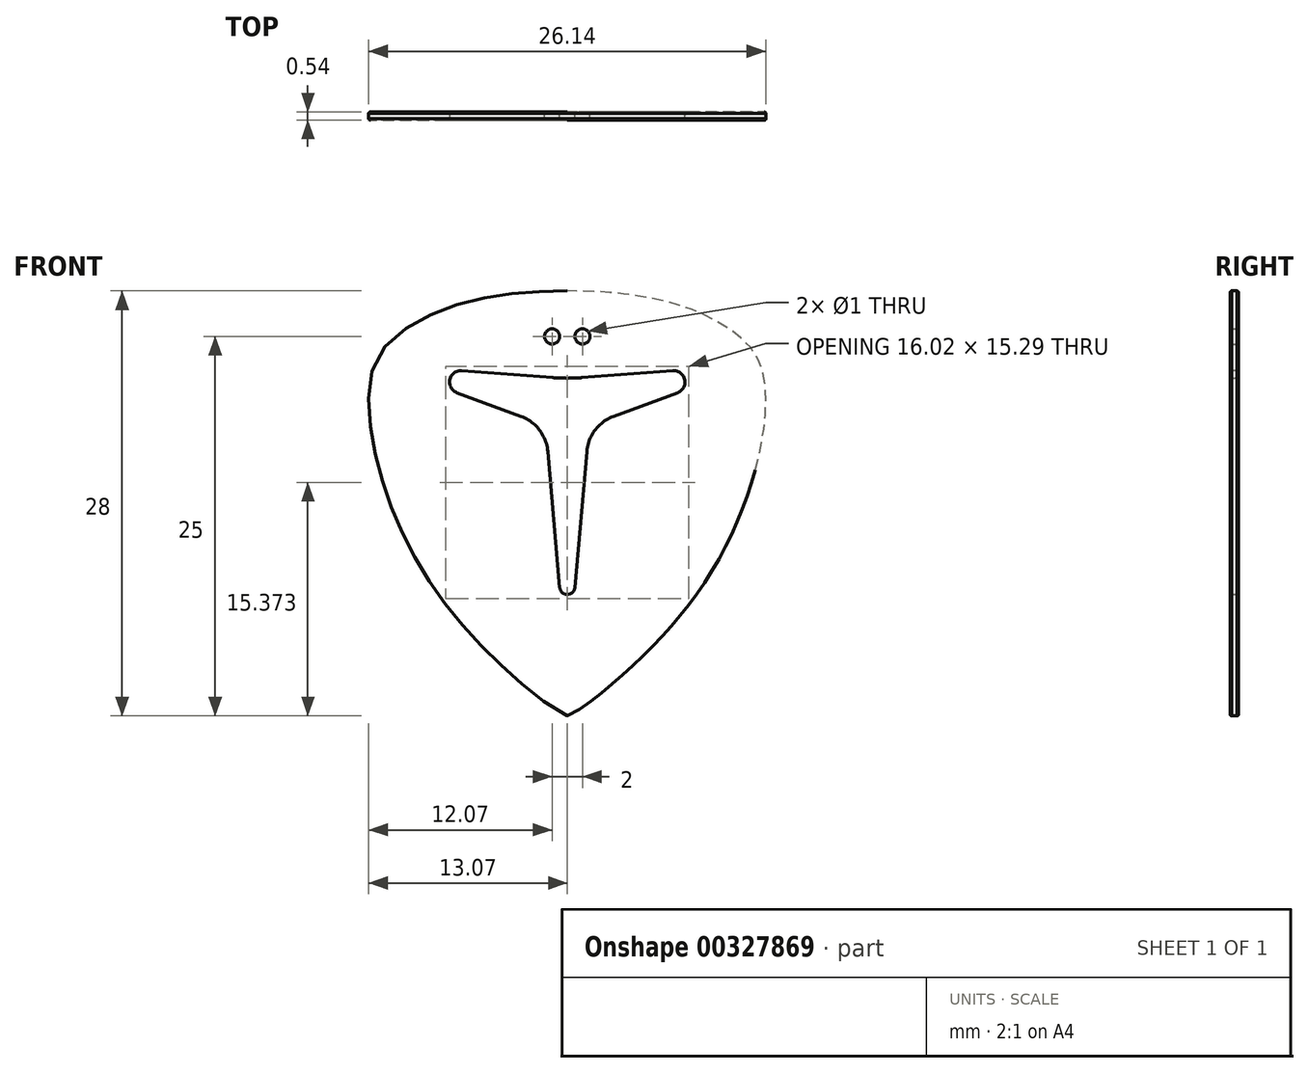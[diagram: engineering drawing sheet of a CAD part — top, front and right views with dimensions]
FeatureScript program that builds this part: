
annotation { "Feature Type Name" : "Feature", "Feature Type Description" : "" }
export const myFeature = defineFeature(function(context is Context, id is Id, definition is map)
    precondition{}
    {
        {
            var Q0;
            Q0=qCreatedBy(makeId("Front.planeOp"),FACE);
            var sketch = newSketch(context, id + "F0", { "sketchPlane" : qUnion([Q0])});
            skLineSegment(sketch, "E0", {"start": v(0, 0) * mm, "end": v(0, 6) * mm, "construction": true});
            skLineSegment(sketch, "E1", {"start": v(0, 0) * mm, "end": v(0, -22) * mm, "construction": true});
            skLineSegment(sketch, "E2", {"start": v(0, 0) * mm, "end": v(13, 0) * mm, "construction": true});
            skFitSpline(sketch, "E3", {"points": [v(0, -22) * mm, v(8.5, -14) * mm, v(13, 0) * mm, v(11, 3.25) * mm, v(0, 6) * mm], "startDerivative": vector(5.52, 0) * mm, "endDerivative": vector(-67.2, 0) * mm});
            skFitSpline(sketch, "E4.MirrorCS", {"points": [v(0, -22) * mm, v(-8.5, -14) * mm, v(-13, 0) * mm, v(-11, 3.25) * mm, v(0, 6) * mm], "startDerivative": vector(-5.52, 0) * mm, "endDerivative": vector(67.2, 0) * mm});
            skArc(sketch, "E5", {"start": v(7.26, -0.7) * mm, "mid": v(7.73, 0.16) * mm, "end": v(6.94, 0.75) * mm});
            skLineSegment(sketch, "E6", {"start": v(7.26, -0.7) * mm, "end": v(3.04, -2.27) * mm});
            skArc(sketch, "E7", {"start": v(3.04, -2.27) * mm, "mid": v(1.83, -3.17) * mm, "end": v(1.28, -4.58) * mm});
            skLineSegment(sketch, "E8", {"start": v(0.5, -13.54) * mm, "end": v(1.28, -4.58) * mm});
            skArc(sketch, "E9", {"start": v(0, -14) * mm, "mid": v(0.34, -13.87) * mm, "end": v(0.5, -13.54) * mm});
            skArc(sketch, "E10.MirrorCS", {"start": v(0, -14) * mm, "mid": v(-0.34, -13.87) * mm, "end": v(-0.5, -13.54) * mm});
            skLineSegment(sketch, "E11.MirrorCS", {"start": v(-0.5, -13.54) * mm, "end": v(-1.28, -4.58) * mm});
            skArc(sketch, "E12.MirrorCS", {"start": v(-3.04, -2.27) * mm, "mid": v(-1.83, -3.17) * mm, "end": v(-1.28, -4.58) * mm});
            skLineSegment(sketch, "E13.MirrorCS", {"start": v(-7.26, -0.7) * mm, "end": v(-3.04, -2.27) * mm});
            skArc(sketch, "E14.MirrorCS", {"start": v(-7.26, -0.7) * mm, "mid": v(-7.73, 0.16) * mm, "end": v(-6.94, 0.75) * mm});
            skLineSegment(sketch, "E15", {"start": v(6.94, 0.75) * mm, "end": v(0.96, 0.29) * mm});
            skArc(sketch, "E16", {"start": v(0, 0.25) * mm, "mid": v(0.48, 0.26) * mm, "end": v(0.96, 0.29) * mm});
            skArc(sketch, "E17.MirrorCS", {"start": v(0, 0.25) * mm, "mid": v(-0.48, 0.26) * mm, "end": v(-0.96, 0.29) * mm});
            skLineSegment(sketch, "E18.MirrorCS", {"start": v(-6.94, 0.75) * mm, "end": v(-0.96, 0.29) * mm});
            skLineSegment(sketch, "E19", {"start": v(0, 3) * mm, "end": v(1, 3) * mm});
            skCircle(sketch, "E20", {"center": v(1, 3) * mm, "radius": 0.5 * mm});
            skCircle(sketch, "E21.MirrorC", {"center": v(-1, 3) * mm, "radius": 0.5 * mm});
            skLineSegment(sketch, "E22.MirrorCS", {"start": v(0, 3) * mm, "end": v(-1, 3) * mm});
            skSolve(sketch);
        }
        {
            var Q0;
            Q0=qSketchRegion(id+"F0",true);
            extrude(context, id + "F1", {"entities" : qUnion([Q0]), "depth" : 0.54 * mm});
        }
        {
            var Q0;
            Q0=makeQuery(id+"F1.opExtrude","CAP_EDGE",EDGE,{"disambiguationData":[OSD([sQuery(id+"F0.wireOp",EDGE,"E5")])],"isStart":false});
            var Q1;
            Q1=makeQuery(id+"F1.opExtrude","CAP_EDGE",EDGE,{"disambiguationData":[OSD([sQuery(id+"F0.wireOp",EDGE,"E7")])],"isStart":true});
            var Q2;
            Q2=makeQuery(id+"F1.opExtrude","CAP_EDGE",EDGE,{"disambiguationData":[OSD([sQuery(id+"F0.wireOp",EDGE,"E9"),sQuery(id+"F0.wireOp",EDGE,"E10.MirrorCS")])],"isStart":false});
            var Q3;
            Q3=makeQuery(id+"F1.opExtrude","CAP_EDGE",EDGE,{"disambiguationData":[OSD([sQuery(id+"F0.wireOp",EDGE,"E14.MirrorCS")])],"isStart":false});
            var Q4;
            Q4=makeQuery(id+"F1.opExtrude","CAP_EDGE",EDGE,{"disambiguationData":[OSD([sQuery(id+"F0.wireOp",EDGE,"E5")])],"isStart":true});
            var Q5;
            Q5=makeQuery(id+"F1.opExtrude","CAP_EDGE",EDGE,{"disambiguationData":[OSD([sQuery(id+"F0.wireOp",EDGE,"E12.MirrorCS")])],"isStart":false});
            var Q6;
            Q6=makeQuery(id+"F1.opExtrude","CAP_EDGE",EDGE,{"disambiguationData":[OSD([sQuery(id+"F0.wireOp",EDGE,"E7")])],"isStart":false});
            var Q7;
            Q7=makeQuery(id+"F1.opExtrude","CAP_EDGE",EDGE,{"disambiguationData":[OSD([sQuery(id+"F0.wireOp",EDGE,"cP70XH3B-hxny-nh1n-TbyW-52Zl4TOD4HrO"),sQuery(id+"F0.wireOp",EDGE,"9cf6c757-e815-40dd-95a7-672993b90d513.MirrorCS")])],"isStart":true});
            var Q8;
            Q8=makeQuery(id+"F1.opExtrude","CAP_EDGE",EDGE,{"disambiguationData":[OSD([sQuery(id+"F0.wireOp",EDGE,"E13.MirrorCS")])],"isStart":false});
            var Q9;
            Q9=makeQuery(id+"F1.opExtrude","CAP_EDGE",EDGE,{"disambiguationData":[OSD([sQuery(id+"F0.wireOp",EDGE,"E12.MirrorCS")])],"isStart":true});
            var Q10;
            Q10=makeQuery(id+"F1.opExtrude","CAP_EDGE",EDGE,{"disambiguationData":[OSD([sQuery(id+"F0.wireOp",EDGE,"cP70XH3B-hxny-nh1n-TbyW-52Zl4TOD4HrO"),sQuery(id+"F0.wireOp",EDGE,"9cf6c757-e815-40dd-95a7-672993b90d513.MirrorCS")])],"isStart":false});
            var Q11;
            Q11=makeQuery(id+"F1.opExtrude","CAP_EDGE",EDGE,{"disambiguationData":[OSD([sQuery(id+"F0.wireOp",EDGE,"E9"),sQuery(id+"F0.wireOp",EDGE,"E10.MirrorCS")])],"isStart":true});
            var Q12;
            Q12=makeQuery(id+"F1.opExtrude","SWEPT_EDGE",EDGE,{"disambiguationData":[OSD([sQuery(id+"F0.wireOp",EDGE,"9cf6c757-e815-40dd-95a7-672993b90d513.MirrorCS"),sQuery(id+"F0.wireOp",EDGE,"E14.MirrorCS")])]});
            var Q13;
            Q13=makeQuery(id+"F1.opExtrude","CAP_EDGE",EDGE,{"disambiguationData":[OSD([sQuery(id+"F0.wireOp",EDGE,"E8")])],"isStart":true});
            var Q14;
            Q14=makeQuery(id+"F1.opExtrude","CAP_EDGE",EDGE,{"disambiguationData":[OSD([sQuery(id+"F0.wireOp",EDGE,"E11.MirrorCS")])],"isStart":false});
            var Q15;
            Q15=makeQuery(id+"F1.opExtrude","SWEPT_EDGE",EDGE,{"disambiguationData":[OSD([sQuery(id+"F0.wireOp",EDGE,"E6"),sQuery(id+"F0.wireOp",EDGE,"E7")])]});
            var Q16;
            Q16=makeQuery(id+"F1.opExtrude","SWEPT_EDGE",EDGE,{"disambiguationData":[OSD([sQuery(id+"F0.wireOp",EDGE,"E8"),sQuery(id+"F0.wireOp",EDGE,"E9")])]});
            var Q17;
            Q17=makeQuery(id+"F1.opExtrude","SWEPT_EDGE",EDGE,{"disambiguationData":[OSD([sQuery(id+"F0.wireOp",EDGE,"E13.MirrorCS"),sQuery(id+"F0.wireOp",EDGE,"E14.MirrorCS")])]});
            var Q18;
            Q18=makeQuery(id+"F1.opExtrude","SWEPT_EDGE",EDGE,{"disambiguationData":[OSD([sQuery(id+"F0.wireOp",EDGE,"E10.MirrorCS"),sQuery(id+"F0.wireOp",EDGE,"E11.MirrorCS")])]});
            var Q19;
            Q19=makeQuery(id+"F1.opExtrude","SWEPT_EDGE",EDGE,{"disambiguationData":[OSD([sQuery(id+"F0.wireOp",EDGE,"E11.MirrorCS"),sQuery(id+"F0.wireOp",EDGE,"E12.MirrorCS")])]});
            var Q20;
            Q20=makeQuery(id+"F1.opExtrude","SWEPT_EDGE",EDGE,{"disambiguationData":[OSD([sQuery(id+"F0.wireOp",EDGE,"E5"),sQuery(id+"F0.wireOp",EDGE,"E6")])]});
            var Q21;
            Q21=makeQuery(id+"F1.opExtrude","CAP_EDGE",EDGE,{"disambiguationData":[OSD([sQuery(id+"F0.wireOp",EDGE,"E14.MirrorCS")])],"isStart":true});
            var Q22;
            Q22=makeQuery(id+"F1.opExtrude","SWEPT_EDGE",EDGE,{"disambiguationData":[OSD([sQuery(id+"F0.wireOp",EDGE,"E12.MirrorCS"),sQuery(id+"F0.wireOp",EDGE,"E13.MirrorCS")])]});
            var Q23;
            Q23=makeQuery(id+"F1.opExtrude","CAP_EDGE",EDGE,{"disambiguationData":[OSD([sQuery(id+"F0.wireOp",EDGE,"E8")])],"isStart":false});
            var Q24;
            Q24=makeQuery(id+"F1.opExtrude","SWEPT_EDGE",EDGE,{"disambiguationData":[OSD([sQuery(id+"F0.wireOp",EDGE,"cP70XH3B-hxny-nh1n-TbyW-52Zl4TOD4HrO"),sQuery(id+"F0.wireOp",EDGE,"E5")])]});
            var Q25;
            Q25=makeQuery(id+"F1.opExtrude","CAP_EDGE",EDGE,{"disambiguationData":[OSD([sQuery(id+"F0.wireOp",EDGE,"E6")])],"isStart":false});
            var Q26;
            Q26=makeQuery(id+"F1.opExtrude","CAP_EDGE",EDGE,{"disambiguationData":[OSD([sQuery(id+"F0.wireOp",EDGE,"E11.MirrorCS")])],"isStart":true});
            var Q27;
            Q27=makeQuery(id+"F1.opExtrude","SWEPT_EDGE",EDGE,{"disambiguationData":[OSD([sQuery(id+"F0.wireOp",EDGE,"E7"),sQuery(id+"F0.wireOp",EDGE,"E8")])]});
            var Q28;
            Q28=makeQuery(id+"F1.opExtrude","CAP_EDGE",EDGE,{"disambiguationData":[OSD([sQuery(id+"F0.wireOp",EDGE,"E6")])],"isStart":true});
            var Q29;
            Q29=makeQuery(id+"F1.opExtrude","CAP_EDGE",EDGE,{"disambiguationData":[OSD([sQuery(id+"F0.wireOp",EDGE,"E13.MirrorCS")])],"isStart":true});
            var Q30;
            Q30=makeQuery(id+"F1.opExtrude","CAP_EDGE",EDGE,{"disambiguationData":[OSD([sQuery(id+"F0.wireOp",EDGE,"E18.MirrorCS")])],"isStart":false});
            var Q31;
            Q31=makeQuery(id+"F1.opExtrude","CAP_EDGE",EDGE,{"disambiguationData":[OSD([sQuery(id+"F0.wireOp",EDGE,"E18.MirrorCS")])],"isStart":true});
            var Q32;
            Q32=makeQuery(id+"F1.opExtrude","CAP_EDGE",EDGE,{"disambiguationData":[OSD([sQuery(id+"F0.wireOp",EDGE,"E16"),sQuery(id+"F0.wireOp",EDGE,"E17.MirrorCS")])],"isStart":false});
            var Q33;
            Q33=makeQuery(id+"F1.opExtrude","CAP_EDGE",EDGE,{"disambiguationData":[OSD([sQuery(id+"F0.wireOp",EDGE,"E16"),sQuery(id+"F0.wireOp",EDGE,"E17.MirrorCS")])],"isStart":true});
            var Q34;
            Q34=makeQuery(id+"F1.opExtrude","CAP_EDGE",EDGE,{"disambiguationData":[OSD([sQuery(id+"F0.wireOp",EDGE,"E15")])],"isStart":false});
            fillet(context, id + "F2", {"entities" : qUnion([Q0, Q1, Q2, Q3, Q4, Q5, Q6, Q7, Q8, Q9, Q10, Q11, Q12, Q13, Q14, Q15, Q16, Q17, Q18, Q19, Q20, Q21, Q22, Q23, Q24, Q25, Q26, Q27, Q28, Q29, Q30, Q31, Q32, Q33, Q34]), "radius" : (0.54 / 2) * mm, "tangentPropagation" : true, "allowEdgeOverflow" : false});
        }
        {
            var Q0;
            Q0=makeQuery(id+"F1.opExtrude","CAP_EDGE",EDGE,{"disambiguationData":[OSD([sQuery(id+"F0.wireOp",EDGE,"E3")])],"isStart":false});
            var Q1;
            Q1=makeQuery(id+"F1.opExtrude","CAP_EDGE",EDGE,{"disambiguationData":[OSD([sQuery(id+"F0.wireOp",EDGE,"E4.MirrorCS")])],"isStart":false});
            var Q2;
            Q2=makeQuery(id+"F1.opExtrude","CAP_EDGE",EDGE,{"disambiguationData":[OSD([sQuery(id+"F0.wireOp",EDGE,"E4.MirrorCS")])],"isStart":true});
            var Q3;
            Q3=makeQuery(id+"F1.opExtrude","CAP_EDGE",EDGE,{"disambiguationData":[OSD([sQuery(id+"F0.wireOp",EDGE,"E3")])],"isStart":true});
            fillet(context, id + "F3", {"entities" : qUnion([Q0, Q1, Q2, Q3]), "radius" : 0.1 * mm, "tangentPropagation" : true, "allowEdgeOverflow" : false});
        }
    });
